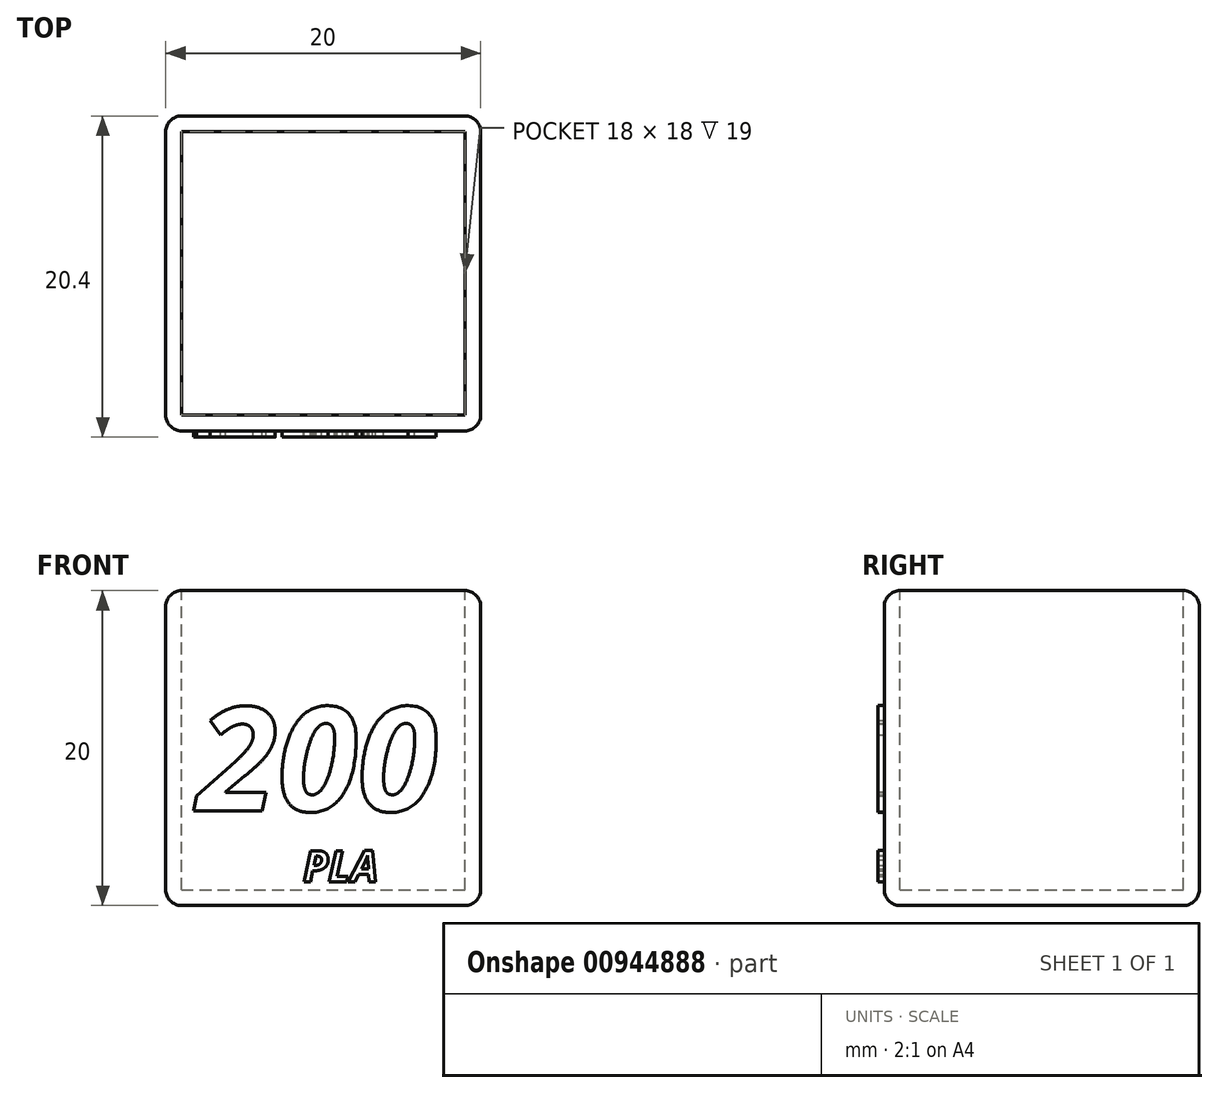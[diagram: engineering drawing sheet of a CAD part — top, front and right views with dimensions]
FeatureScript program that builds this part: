
annotation { "Feature Type Name" : "Feature", "Feature Type Description" : "" }
export const myFeature = defineFeature(function(context is Context, id is Id, definition is map)
    precondition{}
    {
        {
            var Q0;
            Q0=qCreatedBy(makeId("Top.planeOp"),FACE);
            var sketch = newSketch(context, id + "F0", { "sketchPlane" : qUnion([Q0])});
            skLineSegment(sketch, "E0.bottom", {"start": v(10, -10) * mm, "end": v(-10, -10) * mm});
            skLineSegment(sketch, "E0.top", {"start": v(10, 10) * mm, "end": v(-10, 10) * mm});
            skLineSegment(sketch, "E0.left", {"start": v(10, -10) * mm, "end": v(10, 10) * mm});
            skLineSegment(sketch, "E0.right", {"start": v(-10, -10) * mm, "end": v(-10, 10) * mm});
            skPoint(sketch, "E0.middle", {"position": v(0, 0) * mm});
            skSolve(sketch);
        }
        {
            var Q0;
            Q0=qSketchRegion(id+"F0",true);
            extrude(context, id + "F1", {"entities" : qUnion([Q0]), "depth" : 20 * mm, "offsetDistance" : 25 * mm});
        }
        {
            var Q0;
            Q0=makeQuery(id+"F1.opExtrude","SWEPT_EDGE",EDGE,{"disambiguationData":[OSD([sQuery(id+"F0.wireOp",EDGE,"E0.top"),sQuery(id+"F0.wireOp",EDGE,"E0.left")])]});
            var Q1;
            Q1=makeQuery(id+"F1.opExtrude","SWEPT_EDGE",EDGE,{"disambiguationData":[OSD([sQuery(id+"F0.wireOp",EDGE,"E0.bottom"),sQuery(id+"F0.wireOp",EDGE,"E0.right")])]});
            var Q2;
            Q2=makeQuery(id+"F1.opExtrude","SWEPT_EDGE",EDGE,{"disambiguationData":[OSD([sQuery(id+"F0.wireOp",EDGE,"E0.bottom"),sQuery(id+"F0.wireOp",EDGE,"E0.left")])]});
            var Q3;
            Q3=makeQuery(id+"F1.opExtrude","SWEPT_EDGE",EDGE,{"disambiguationData":[OSD([sQuery(id+"F0.wireOp",EDGE,"E0.top"),sQuery(id+"F0.wireOp",EDGE,"E0.right")])]});
            var Q4;
            Q4=makeQuery(id+"F1.opExtrude","CAP_EDGE",EDGE,{"disambiguationData":[OSD([sQuery(id+"F0.wireOp",EDGE,"E0.left")])],"isStart":true});
            var Q5;
            Q5=makeQuery(id+"F1.opExtrude","CAP_EDGE",EDGE,{"disambiguationData":[OSD([sQuery(id+"F0.wireOp",EDGE,"E0.bottom")])],"isStart":true});
            var Q6;
            Q6=makeQuery(id+"F1.opExtrude","CAP_EDGE",EDGE,{"disambiguationData":[OSD([sQuery(id+"F0.wireOp",EDGE,"E0.top")])],"isStart":true});
            var Q7;
            Q7=makeQuery(id+"F1.opExtrude","CAP_EDGE",EDGE,{"disambiguationData":[OSD([sQuery(id+"F0.wireOp",EDGE,"E0.right")])],"isStart":true});
            fillet(context, id + "F2", {"entities" : qUnion([Q0, Q1, Q2, Q3, Q4, Q5, Q6, Q7]), "radius" : 1 * mm, "tangentPropagation" : true, "allowEdgeOverflow" : false});
        }
        {
            var Q0;
            Q0=makeQuery(id+"F1.opExtrude","CAP_FACE",FACE,{"disambiguationData":[OSD([sQuery(id+"F0.wireOp",EDGE,"E0.bottom"),sQuery(id+"F0.wireOp",EDGE,"E0.top"),sQuery(id+"F0.wireOp",EDGE,"E0.left"),sQuery(id+"F0.wireOp",EDGE,"E0.right")])],"isStart":false});
            shell(context, id + "F3", {"entities" : qUnion([Q0]), "thickness" : 1 * mm});
        }
        {
            var Q0;
            {var subQ0=sQuery(id+"F0.wireOp",EDGE,"E0.left");var subQ1=sQuery(id+"F0.wireOp",EDGE,"E0.top");Q0=makeQuery(id+"F2.opFillet","BLEND_EDGE",EDGE,{"blendedFrom":[makeQuery(id+"F1.opExtrude","SWEPT_EDGE",EDGE,{"disambiguationData":[OSD([subQ1,subQ0])]}),makeQuery(id+"F1.opExtrude","CAP_FACE",FACE,{"disambiguationData":[OSD([sQuery(id+"F0.wireOp",EDGE,"E0.bottom"),subQ1,subQ0,sQuery(id+"F0.wireOp",EDGE,"E0.right")])],"isStart":false})],"blendedInto":[makeQuery(id+"F1.opExtrude","CAP_FACE",FACE,{"disambiguationData":[OSD([sQuery(id+"F0.wireOp",EDGE,"E0.bottom"),subQ1,subQ0,sQuery(id+"F0.wireOp",EDGE,"E0.right")])],"isStart":false})]});}
            var Q1;
            {var subQ0=sQuery(id+"F0.wireOp",EDGE,"E0.right");var subQ1=sQuery(id+"F0.wireOp",EDGE,"E0.top");Q1=makeQuery(id+"F2.opFillet","BLEND_EDGE",EDGE,{"blendedFrom":[makeQuery(id+"F1.opExtrude","SWEPT_EDGE",EDGE,{"disambiguationData":[OSD([subQ1,subQ0])]}),makeQuery(id+"F1.opExtrude","CAP_FACE",FACE,{"disambiguationData":[OSD([sQuery(id+"F0.wireOp",EDGE,"E0.bottom"),subQ1,sQuery(id+"F0.wireOp",EDGE,"E0.left"),subQ0])],"isStart":false})],"blendedInto":[makeQuery(id+"F1.opExtrude","CAP_FACE",FACE,{"disambiguationData":[OSD([sQuery(id+"F0.wireOp",EDGE,"E0.bottom"),subQ1,sQuery(id+"F0.wireOp",EDGE,"E0.left"),subQ0])],"isStart":false})]});}
            var Q2;
            Q2=makeQuery(id+"F1.opExtrude","CAP_EDGE",EDGE,{"disambiguationData":[OSD([sQuery(id+"F0.wireOp",EDGE,"E0.bottom")])],"isStart":false});
            var Q3;
            Q3=makeQuery(id+"F1.opExtrude","CAP_EDGE",EDGE,{"disambiguationData":[OSD([sQuery(id+"F0.wireOp",EDGE,"E0.top")])],"isStart":false});
            var Q4;
            {var subQ0=sQuery(id+"F0.wireOp",EDGE,"E0.right");var subQ1=sQuery(id+"F0.wireOp",EDGE,"E0.bottom");Q4=makeQuery(id+"F2.opFillet","BLEND_EDGE",EDGE,{"blendedFrom":[makeQuery(id+"F1.opExtrude","SWEPT_EDGE",EDGE,{"disambiguationData":[OSD([subQ1,subQ0])]}),makeQuery(id+"F1.opExtrude","CAP_FACE",FACE,{"disambiguationData":[OSD([subQ1,sQuery(id+"F0.wireOp",EDGE,"E0.top"),sQuery(id+"F0.wireOp",EDGE,"E0.left"),subQ0])],"isStart":false})],"blendedInto":[makeQuery(id+"F1.opExtrude","CAP_FACE",FACE,{"disambiguationData":[OSD([subQ1,sQuery(id+"F0.wireOp",EDGE,"E0.top"),sQuery(id+"F0.wireOp",EDGE,"E0.left"),subQ0])],"isStart":false})]});}
            var Q5;
            Q5=makeQuery(id+"F1.opExtrude","CAP_EDGE",EDGE,{"disambiguationData":[OSD([sQuery(id+"F0.wireOp",EDGE,"E0.left")])],"isStart":false});
            var Q6;
            Q6=makeQuery(id+"F1.opExtrude","CAP_EDGE",EDGE,{"disambiguationData":[OSD([sQuery(id+"F0.wireOp",EDGE,"E0.right")])],"isStart":false});
            var Q7;
            {var subQ0=sQuery(id+"F0.wireOp",EDGE,"E0.left");var subQ1=sQuery(id+"F0.wireOp",EDGE,"E0.bottom");Q7=makeQuery(id+"F2.opFillet","BLEND_EDGE",EDGE,{"blendedFrom":[makeQuery(id+"F1.opExtrude","SWEPT_EDGE",EDGE,{"disambiguationData":[OSD([subQ1,subQ0])]}),makeQuery(id+"F1.opExtrude","CAP_FACE",FACE,{"disambiguationData":[OSD([subQ1,sQuery(id+"F0.wireOp",EDGE,"E0.top"),subQ0,sQuery(id+"F0.wireOp",EDGE,"E0.right")])],"isStart":false})],"blendedInto":[makeQuery(id+"F1.opExtrude","CAP_FACE",FACE,{"disambiguationData":[OSD([subQ1,sQuery(id+"F0.wireOp",EDGE,"E0.top"),subQ0,sQuery(id+"F0.wireOp",EDGE,"E0.right")])],"isStart":false})]});}
            fillet(context, id + "F4", {"entities" : qUnion([Q0, Q1, Q2, Q3, Q4, Q5, Q6, Q7]), "radius" : 1 * mm, "tangentPropagation" : true, "allowEdgeOverflow" : false});
        }
        {
            var Q0;
            Q0=makeQuery(id+"F1.opExtrude","SWEPT_FACE",FACE,{"disambiguationData":[OSD([sQuery(id+"F0.wireOp",EDGE,"E0.right")])]});
            var sketch = newSketch(context, id + "F5", { "sketchPlane" : qUnion([Q0])});
            skLineSegment(sketch, "E1", {"start": v(-9, 10) * mm, "end": v(0, 19) * mm});
            skLineSegment(sketch, "E2", {"start": v(0, 19) * mm, "end": v(9, 10) * mm});
            skLineSegment(sketch, "E3", {"start": v(9, 10) * mm, "end": v(0, 1) * mm});
            skLineSegment(sketch, "E4", {"start": v(0, 1) * mm, "end": v(-9, 10) * mm});
            skSolve(sketch);
        }
        {
            var Q0;
            Q0=makeQuery(id+"F1.opExtrude","SWEPT_FACE",FACE,{"disambiguationData":[OSD([sQuery(id+"F0.wireOp",EDGE,"E0.top")])]});
            var sketch = newSketch(context, id + "F6", { "sketchPlane" : qUnion([Q0])});
            skLineSegment(sketch, "E5", {"start": v(-9, 10) * mm, "end": v(0, 19) * mm});
            skLineSegment(sketch, "E6", {"start": v(0, 19) * mm, "end": v(9, 10) * mm});
            skLineSegment(sketch, "E7", {"start": v(9, 10) * mm, "end": v(0, 1) * mm});
            skLineSegment(sketch, "E8", {"start": v(0, 1) * mm, "end": v(-9, 10) * mm});
            skSolve(sketch);
        }
        {
            var Q0;
            Q0=makeQuery(id+"F1.opExtrude","SWEPT_FACE",FACE,{"disambiguationData":[OSD([sQuery(id+"F0.wireOp",EDGE,"E0.bottom")])]});
            var sketch = newSketch(context, id + "F7", { "sketchPlane" : qUnion([Q0])});
            skText(sketch, "E9", { "text": "200", "fontName": "OpenSans-BoldItalic.ttf"});
            const initialGuessF7  = {"E9": [-0.008, 0.006, 1, 0, 0.00665]};
            skSetInitialGuess(sketch, initialGuessF7);
            skSolve(sketch);
        }
        {
            var Q0;
            Q0=qSketchRegion(id+"F7",true);
            extrude(context, id + "F8", {"entities" : qUnion([Q0]), "operationType" : NewBodyOperationType.ADD, "depth" : 0.4 * mm, "offsetDistance" : 25 * mm});
        }
        {
            var Q0;
            {var subQ0=sQuery(id+"F0.wireOp",EDGE,"E0.bottom");Q0=makeQuery(id+"F8.boolean.opBoolean","SPLIT",FACE,{"disambiguationData":[TD([makeQuery(id+"F2.opFillet","BLEND_FACE",FACE,{"disambiguationData":[OSD([subQ0])]})])],"derivedFrom":makeQuery(id+"F1.opExtrude","SWEPT_FACE",FACE,{"disambiguationData":[OSD([subQ0])]})});}
            var sketch = newSketch(context, id + "F9", { "sketchPlane" : qUnion([Q0])});
            skText(sketch, "E10", { "text": "PLA", "fontName": "OpenSans-BoldItalic.ttf"});
            const initialGuessF9  = {"E10": [-0.0013, 0.0015, 1, 0, 0.002]};
            skSetInitialGuess(sketch, initialGuessF9);
            skSolve(sketch);
        }
        {
            var Q0;
            Q0=qSketchRegion(id+"F9",true);
            extrude(context, id + "F10", {"entities" : qUnion([Q0]), "operationType" : NewBodyOperationType.ADD, "depth" : 0.4 * mm, "offsetDistance" : 25 * mm});
        }
    });
